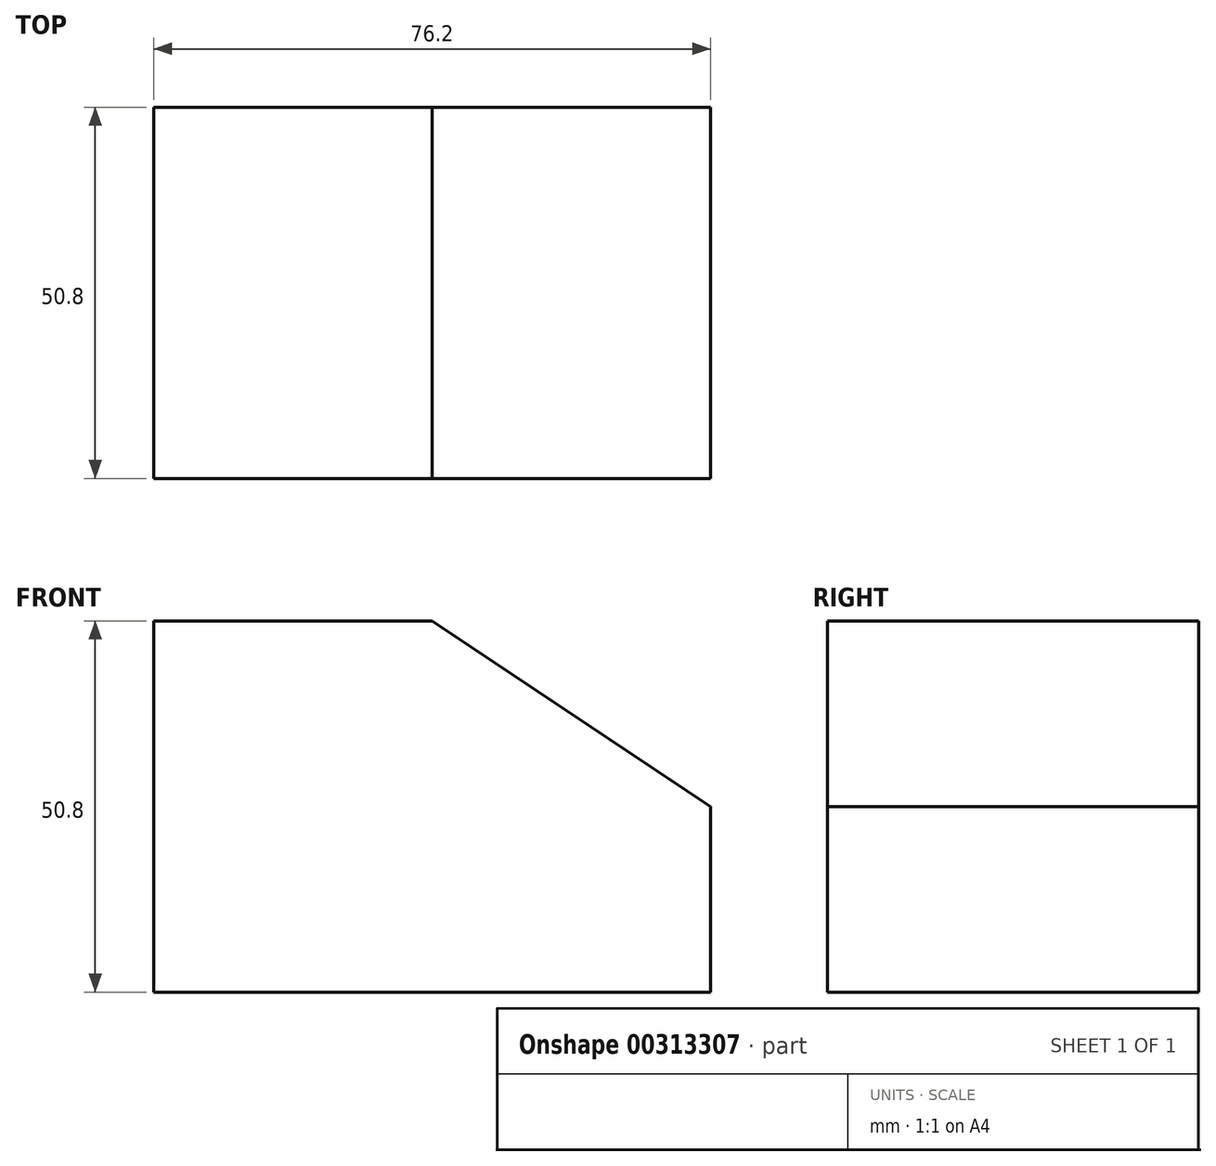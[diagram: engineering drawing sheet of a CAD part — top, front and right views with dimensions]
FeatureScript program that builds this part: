
annotation { "Feature Type Name" : "Feature", "Feature Type Description" : "" }
export const myFeature = defineFeature(function(context is Context, id is Id, definition is map)
    precondition{}
    {
        {
            var Q0;
            Q0=qCreatedBy(makeId("Front.planeOp"),FACE);
            var sketch = newSketch(context, id + "F0", { "sketchPlane" : qUnion([Q0])});
            skLineSegment(sketch, "E0", {"start": v(-44.8, -33.32) * mm, "end": v(31.4, -33.32) * mm});
            skLineSegment(sketch, "E1", {"start": v(31.4, -33.32) * mm, "end": v(31.4, -7.92) * mm});
            skLineSegment(sketch, "E2", {"start": v(31.4, -7.92) * mm, "end": v(-6.7, 17.48) * mm});
            skLineSegment(sketch, "E3", {"start": v(-6.7, 17.48) * mm, "end": v(-44.8, 17.48) * mm});
            skLineSegment(sketch, "E4", {"start": v(-44.8, 17.48) * mm, "end": v(-44.8, -33.32) * mm});
            skSolve(sketch);
        }
        {
            var Q0;
            Q0 = qSketchRegion(id + "F0", true);
            extrude(context, id + "F1", {"entities" : qUnion([Q0]), "depth" : 50.8 * mm});
        }
    });
